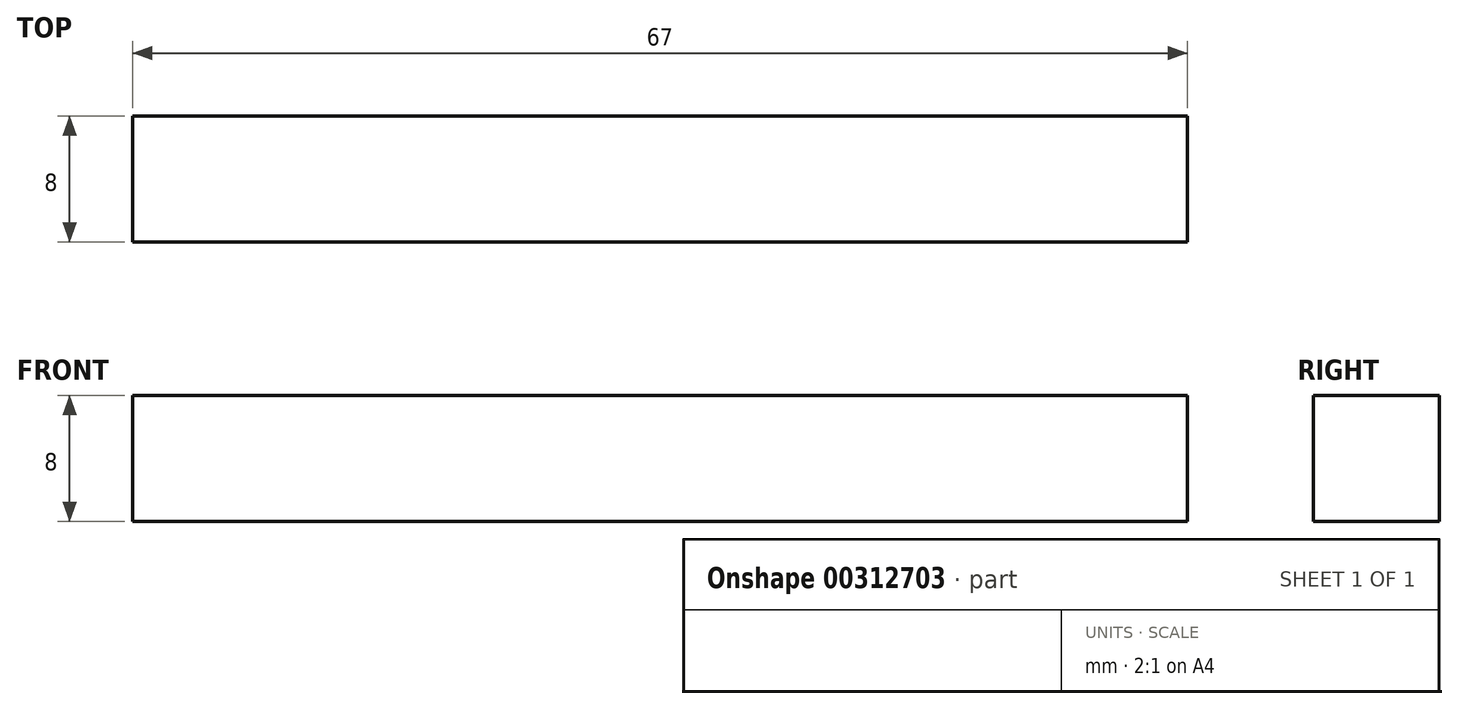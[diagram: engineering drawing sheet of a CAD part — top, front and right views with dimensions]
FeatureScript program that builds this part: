
annotation { "Feature Type Name" : "Feature", "Feature Type Description" : "" }
export const myFeature = defineFeature(function(context is Context, id is Id, definition is map)
    precondition{}
    {
        {
            var Q0;
            Q0=qCreatedBy(makeId("Top.planeOp"),FACE);
            var sketch = newSketch(context, id + "F0", { "sketchPlane" : qUnion([Q0])});
            skLineSegment(sketch, "E0.bottom", {"start": v(-24.76, -21.24) * mm, "end": v(42.24, -21.24) * mm});
            skLineSegment(sketch, "E0.top", {"start": v(-24.76, -29.24) * mm, "end": v(42.24, -29.24) * mm});
            skLineSegment(sketch, "E0.left", {"start": v(-24.76, -21.24) * mm, "end": v(-24.76, -29.24) * mm});
            skLineSegment(sketch, "E0.right", {"start": v(42.24, -21.24) * mm, "end": v(42.24, -29.24) * mm});
            skSolve(sketch);
        }
        {
            var Q0;
            Q0=makeQuery(id+"F0.imprint","IMPRINT",FACE,{"disambiguationData":[TD([[makeQuery(id+"F0.imprint","IMPRINT",EDGE,{"derivedFrom":sQuery(id+"F0.wireOp",EDGE,"E0.bottom")}),-1.0]])]});
            extrude(context, id + "F1", {"entities" : qUnion([Q0]), "depth" : 8 * mm});
        }
    });
